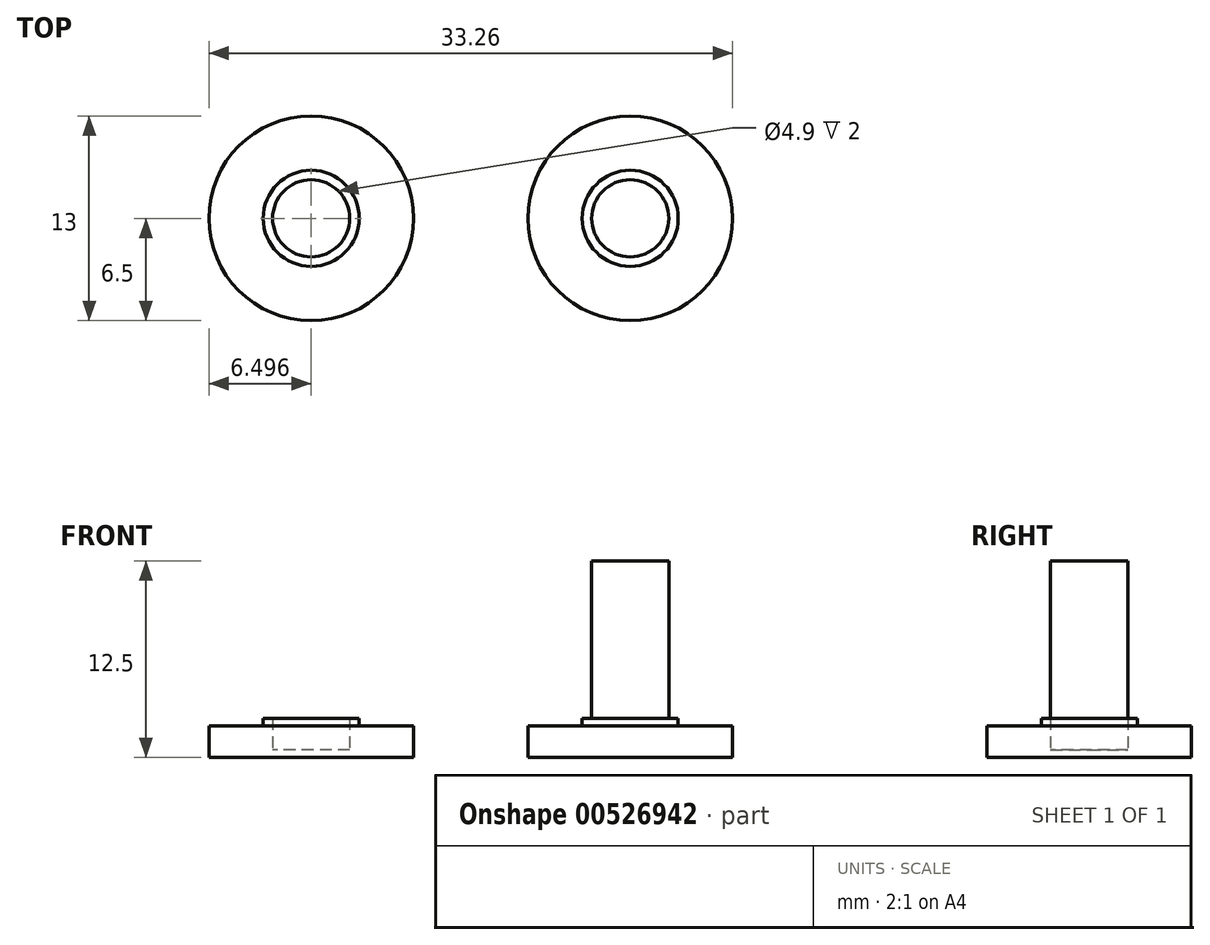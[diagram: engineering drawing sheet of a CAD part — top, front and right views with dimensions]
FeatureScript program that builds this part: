
annotation { "Feature Type Name" : "Feature", "Feature Type Description" : "" }
export const myFeature = defineFeature(function(context is Context, id is Id, definition is map)
    precondition{}
    {
        {
            var Q0;
            Q0=qCreatedBy(makeId("Top.planeOp"),FACE);
            var sketch = newSketch(context, id + "F0", { "sketchPlane" : qUnion([Q0])});
            skCircle(sketch, "E0", {"center": v(0, 0) * mm, "radius": 2.45 * mm});
            skCircle(sketch, "E1", {"center": v(0, 0) * mm, "radius": 6.5 * mm});
            skCircle(sketch, "E2", {"center": v(0, 0) * mm, "radius": 3.05 * mm});
            skSolve(sketch);
        }
        {
            var Q0;
            Q0=makeQuery(id+"F0.imprint","IMPRINT",FACE,{"disambiguationData":[TD([[makeQuery(id+"F0.imprint","IMPRINT",EDGE,{"derivedFrom":sQuery(id+"F0.wireOp",EDGE,"E0")}),1.0]])]});
            extrude(context, id + "F1", {"entities" : qUnion([Q0]), "depth" : 10.5 * mm, "offsetDistance" : 25 * mm});
        }
        {
            var Q0;
            Q0=makeQuery(id+"F0.imprint","IMPRINT",FACE,{"disambiguationData":[TD([[makeQuery(id+"F0.imprint","IMPRINT",EDGE,{"derivedFrom":sQuery(id+"F0.wireOp",EDGE,"E1")}),1.0]])]});
            var Q1;
            Q1=makeQuery(id+"F0.imprint","IMPRINT",FACE,{"disambiguationData":[TD([[makeQuery(id+"F0.imprint","IMPRINT",EDGE,{"derivedFrom":sQuery(id+"F0.wireOp",EDGE,"E0")}),1.0]])]});
            var Q2;
            Q2=makeQuery(id+"F0.imprint","IMPRINT",FACE,{"disambiguationData":[TD([[makeQuery(id+"F0.imprint","IMPRINT",EDGE,{"derivedFrom":sQuery(id+"F0.wireOp",EDGE,"E0")}),-1.0]])]});
            extrude(context, id + "F2", {"entities" : qUnion([Q0, Q1, Q2]), "operationType" : NewBodyOperationType.ADD, "oppositeDirection" : true, "depth" : 2 * mm, "offsetDistance" : 25 * mm});
        }
        {
            var Q0;
            Q0=makeQuery(id+"F0.imprint","IMPRINT",FACE,{"disambiguationData":[TD([[makeQuery(id+"F0.imprint","IMPRINT",EDGE,{"derivedFrom":sQuery(id+"F0.wireOp",EDGE,"E0")}),-1.0]])]});
            extrude(context, id + "F3", {"entities" : qUnion([Q0]), "operationType" : NewBodyOperationType.ADD, "depth" : .5 * mm, "offsetDistance" : 25 * mm});
        }
        {
            var Q0;
            Q0=qCreatedBy(makeId("Top.planeOp"),FACE);
            var sketch = newSketch(context, id + "F4", { "sketchPlane" : qUnion([Q0])});
            skCircle(sketch, "E3", {"center": v(-20.26, 0) * mm, "radius": 6.5 * mm});
            skCircle(sketch, "E4", {"center": v(-20.26, 0) * mm, "radius": 2.45 * mm});
            skCircle(sketch, "E5", {"center": v(-20.26, 0) * mm, "radius": 3.05 * mm});
            skSolve(sketch);
        }
        {
            var Q0;
            Q0=makeQuery(id+"F4.imprint","IMPRINT",FACE,{"disambiguationData":[TD([[makeQuery(id+"F4.imprint","IMPRINT",EDGE,{"derivedFrom":sQuery(id+"F4.wireOp",EDGE,"E3")}),1.0]])]});
            var Q1;
            Q1=makeQuery(id+"F4.imprint","IMPRINT",FACE,{"disambiguationData":[TD([[makeQuery(id+"F4.imprint","IMPRINT",EDGE,{"derivedFrom":sQuery(id+"F4.wireOp",EDGE,"E4")}),1.0]])]});
            var Q2;
            Q2=makeQuery(id+"F4.imprint","IMPRINT",FACE,{"disambiguationData":[TD([[makeQuery(id+"F4.imprint","IMPRINT",EDGE,{"derivedFrom":sQuery(id+"F4.wireOp",EDGE,"E4")}),-1.0]])]});
            extrude(context, id + "F5", {"entities" : qUnion([Q0, Q1, Q2]), "oppositeDirection" : true, "depth" : 2 * mm, "offsetDistance" : 25 * mm});
        }
        {
            var Q0;
            Q0=makeQuery(id+"F4.imprint","IMPRINT",FACE,{"disambiguationData":[TD([[makeQuery(id+"F4.imprint","IMPRINT",EDGE,{"derivedFrom":sQuery(id+"F4.wireOp",EDGE,"E4")}),-1.0]])]});
            extrude(context, id + "F6", {"entities" : qUnion([Q0]), "operationType" : NewBodyOperationType.ADD, "depth" : .5 * mm, "offsetDistance" : 25 * mm});
        }
        {
            var Q0;
            Q0=makeQuery(id+"F4.imprint","IMPRINT",FACE,{"disambiguationData":[TD([[makeQuery(id+"F4.imprint","IMPRINT",EDGE,{"derivedFrom":sQuery(id+"F4.wireOp",EDGE,"E4")}),1.0]])]});
            extrude(context, id + "F7", {"entities" : qUnion([Q0]), "operationType" : NewBodyOperationType.REMOVE, "oppositeDirection" : true, "depth" : 1.5 * mm, "offsetDistance" : 25 * mm});
        }
    });
